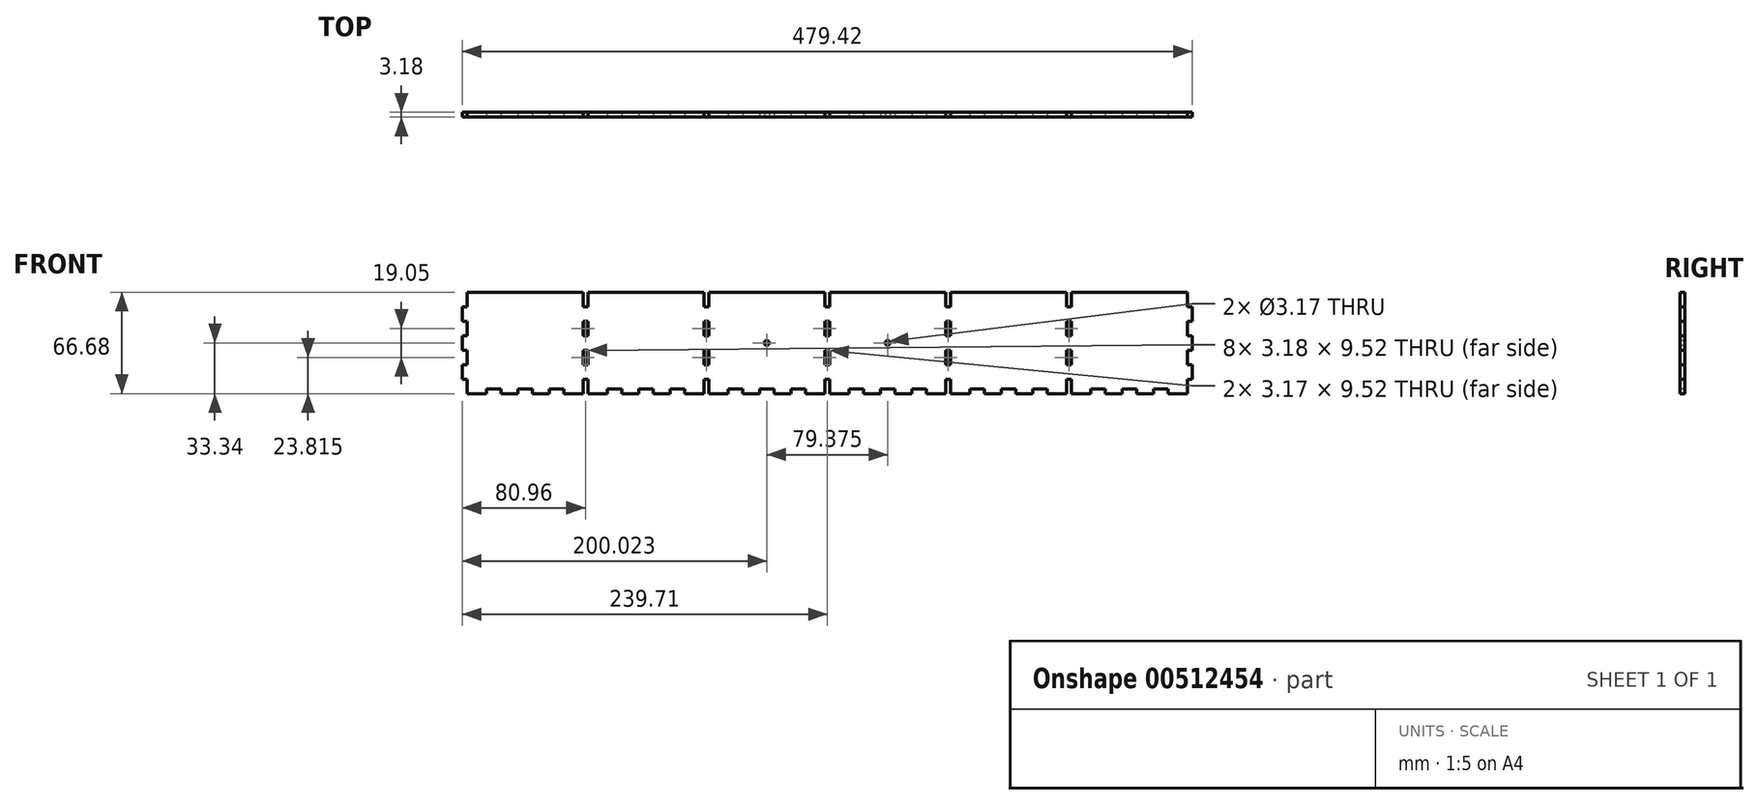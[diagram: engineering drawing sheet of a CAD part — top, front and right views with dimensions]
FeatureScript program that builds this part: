
annotation { "Feature Type Name" : "Feature", "Feature Type Description" : "" }
export const myFeature = defineFeature(function(context is Context, id is Id, definition is map)
    precondition{}
    {
        {
            var Q0;
            Q0=qCreatedBy(makeId("Front.planeOp"),FACE);
            var sketch = newSketch(context, id + "F0", { "sketchPlane" : qUnion([Q0])});
            skLineSegment(sketch, "E0.bottom", {"start": v(-239.71, 33.34) * mm, "end": v(239.71, 33.34) * mm});
            skLineSegment(sketch, "E0.top", {"start": v(-239.71, -33.34) * mm, "end": v(239.71, -33.34) * mm});
            skLineSegment(sketch, "E0.left", {"start": v(-239.71, 33.34) * mm, "end": v(-239.71, -33.34) * mm});
            skLineSegment(sketch, "E0.right", {"start": v(239.71, 33.34) * mm, "end": v(239.71, -33.34) * mm});
            skSolve(sketch);
        }
        {
            var Q0;
            Q0=makeQuery(id+"F0.imprint","IMPRINT",FACE,{"disambiguationData":[TD([[makeQuery(id+"F0.imprint","IMPRINT",EDGE,{"derivedFrom":sQuery(id+"F0.wireOp",EDGE,"E0.bottom")}),-1.0]])]});
            extrude(context, id + "F1", {"entities" : qUnion([Q0]), "depth" : 3.17 * mm});
        }
        {
            var Q0;
            Q0=makeQuery(id+"F1.opExtrude","CAP_FACE",FACE,{"disambiguationData":[OSD([sQuery(id+"F0.wireOp",EDGE,"E0.bottom"),sQuery(id+"F0.wireOp",EDGE,"E0.top"),sQuery(id+"F0.wireOp",EDGE,"E0.left"),sQuery(id+"F0.wireOp",EDGE,"E0.right")])],"isStart":false});
            var sketch = newSketch(context, id + "F2", { "sketchPlane" : qUnion([Q0])});
            skLineSegment(sketch, "E1.bottom", {"start": v(-239.71, -33.34) * mm, "end": v(-236.54, -33.34) * mm});
            skLineSegment(sketch, "E1.top", {"start": v(-239.71, -23.81) * mm, "end": v(-236.54, -23.81) * mm});
            skLineSegment(sketch, "E1.left", {"start": v(-239.71, -33.34) * mm, "end": v(-239.71, -23.81) * mm});
            skLineSegment(sketch, "E1.right", {"start": v(-236.54, -33.34) * mm, "end": v(-236.54, -23.81) * mm});
            skLineSegment(sketch, "E2.0.1.0", {"start": v(-236.54, -14.29) * mm, "end": v(-236.54, -4.76) * mm});
            skLineSegment(sketch, "E2.0.1.1", {"start": v(-239.71, -14.29) * mm, "end": v(-239.71, -4.76) * mm});
            skLineSegment(sketch, "E2.0.1.2", {"start": v(-239.71, -4.76) * mm, "end": v(-236.54, -4.76) * mm});
            skLineSegment(sketch, "E2.0.1.3", {"start": v(-239.71, -14.29) * mm, "end": v(-236.54, -14.29) * mm});
            skLineSegment(sketch, "E2.0.2.0", {"start": v(-236.54, 4.76) * mm, "end": v(-236.54, 14.29) * mm});
            skLineSegment(sketch, "E2.0.2.1", {"start": v(-239.71, 4.76) * mm, "end": v(-239.71, 14.29) * mm});
            skLineSegment(sketch, "E2.0.2.2", {"start": v(-239.71, 14.29) * mm, "end": v(-236.54, 14.29) * mm});
            skLineSegment(sketch, "E2.0.2.3", {"start": v(-239.71, 4.76) * mm, "end": v(-236.54, 4.76) * mm});
            skLineSegment(sketch, "E2.0.3.0", {"start": v(-236.54, 23.81) * mm, "end": v(-236.54, 33.34) * mm});
            skLineSegment(sketch, "E2.0.3.1", {"start": v(-239.71, 23.81) * mm, "end": v(-239.71, 33.34) * mm});
            skLineSegment(sketch, "E2.0.3.2", {"start": v(-239.71, 33.34) * mm, "end": v(-236.54, 33.34) * mm});
            skLineSegment(sketch, "E2.0.3.3", {"start": v(-239.71, 23.81) * mm, "end": v(-236.54, 23.81) * mm});
            skLineSegment(sketch, "E2.1.0.0", {"start": v(-157.16, -33.34) * mm, "end": v(-157.16, -23.81) * mm});
            skLineSegment(sketch, "E2.1.0.1", {"start": v(-160.34, -33.34) * mm, "end": v(-160.34, -23.81) * mm});
            skLineSegment(sketch, "E2.1.0.2", {"start": v(-160.34, -23.81) * mm, "end": v(-157.16, -23.81) * mm});
            skLineSegment(sketch, "E2.1.0.3", {"start": v(-160.34, -33.34) * mm, "end": v(-157.16, -33.34) * mm});
            skLineSegment(sketch, "E2.1.1.0", {"start": v(-157.16, -14.29) * mm, "end": v(-157.16, -4.76) * mm});
            skLineSegment(sketch, "E2.1.1.1", {"start": v(-160.34, -14.29) * mm, "end": v(-160.34, -4.76) * mm});
            skLineSegment(sketch, "E2.1.1.2", {"start": v(-160.34, -4.76) * mm, "end": v(-157.16, -4.76) * mm});
            skLineSegment(sketch, "E2.1.1.3", {"start": v(-160.34, -14.29) * mm, "end": v(-157.16, -14.29) * mm});
            skLineSegment(sketch, "E2.1.2.0", {"start": v(-157.16, 4.76) * mm, "end": v(-157.16, 14.29) * mm});
            skLineSegment(sketch, "E2.1.2.1", {"start": v(-160.34, 4.76) * mm, "end": v(-160.34, 14.29) * mm});
            skLineSegment(sketch, "E2.1.2.2", {"start": v(-160.34, 14.29) * mm, "end": v(-157.16, 14.29) * mm});
            skLineSegment(sketch, "E2.1.2.3", {"start": v(-160.34, 4.76) * mm, "end": v(-157.16, 4.76) * mm});
            skLineSegment(sketch, "E2.1.3.0", {"start": v(-157.16, 23.81) * mm, "end": v(-157.16, 33.34) * mm});
            skLineSegment(sketch, "E2.1.3.1", {"start": v(-160.34, 23.81) * mm, "end": v(-160.34, 33.34) * mm});
            skLineSegment(sketch, "E2.1.3.2", {"start": v(-160.34, 33.34) * mm, "end": v(-157.16, 33.34) * mm});
            skLineSegment(sketch, "E2.1.3.3", {"start": v(-160.34, 23.81) * mm, "end": v(-157.16, 23.81) * mm});
            skLineSegment(sketch, "E2.2.0.0", {"start": v(-77.79, -33.34) * mm, "end": v(-77.79, -23.81) * mm});
            skLineSegment(sketch, "E2.2.0.1", {"start": v(-80.96, -33.34) * mm, "end": v(-80.96, -23.81) * mm});
            skLineSegment(sketch, "E2.2.0.2", {"start": v(-80.96, -23.81) * mm, "end": v(-77.79, -23.81) * mm});
            skLineSegment(sketch, "E2.2.0.3", {"start": v(-80.96, -33.34) * mm, "end": v(-77.79, -33.34) * mm});
            skLineSegment(sketch, "E2.2.1.0", {"start": v(-77.79, -14.29) * mm, "end": v(-77.79, -4.76) * mm});
            skLineSegment(sketch, "E2.2.1.1", {"start": v(-80.96, -14.29) * mm, "end": v(-80.96, -4.76) * mm});
            skLineSegment(sketch, "E2.2.1.2", {"start": v(-80.96, -4.76) * mm, "end": v(-77.79, -4.76) * mm});
            skLineSegment(sketch, "E2.2.1.3", {"start": v(-80.96, -14.29) * mm, "end": v(-77.79, -14.29) * mm});
            skLineSegment(sketch, "E2.2.2.0", {"start": v(-77.79, 4.76) * mm, "end": v(-77.79, 14.29) * mm});
            skLineSegment(sketch, "E2.2.2.1", {"start": v(-80.96, 4.76) * mm, "end": v(-80.96, 14.29) * mm});
            skLineSegment(sketch, "E2.2.2.2", {"start": v(-80.96, 14.29) * mm, "end": v(-77.79, 14.29) * mm});
            skLineSegment(sketch, "E2.2.2.3", {"start": v(-80.96, 4.76) * mm, "end": v(-77.79, 4.76) * mm});
            skLineSegment(sketch, "E2.2.3.0", {"start": v(-77.79, 23.81) * mm, "end": v(-77.79, 33.34) * mm});
            skLineSegment(sketch, "E2.2.3.1", {"start": v(-80.96, 23.81) * mm, "end": v(-80.96, 33.34) * mm});
            skLineSegment(sketch, "E2.2.3.2", {"start": v(-80.96, 33.34) * mm, "end": v(-77.79, 33.34) * mm});
            skLineSegment(sketch, "E2.2.3.3", {"start": v(-80.96, 23.81) * mm, "end": v(-77.79, 23.81) * mm});
            skLineSegment(sketch, "E2.direction1", {"start": v(-239.71, -33.34) * mm, "end": v(-160.34, -33.34) * mm, "construction": true});
            skLineSegment(sketch, "E2.direction2", {"start": v(-239.71, -33.34) * mm, "end": v(-239.71, -14.29) * mm, "construction": true});
            skLineSegment(sketch, "E3.0.3.0", {"start": v(1.59, -33.34) * mm, "end": v(1.59, -23.81) * mm});
            skLineSegment(sketch, "E3.3.3.0", {"start": v(-1.59, -33.34) * mm, "end": v(-1.59, -23.81) * mm});
            skLineSegment(sketch, "E3.6.3.0", {"start": v(-1.59, -23.81) * mm, "end": v(1.59, -23.81) * mm});
            skLineSegment(sketch, "E3.9.3.0", {"start": v(-1.59, -33.34) * mm, "end": v(1.59, -33.34) * mm});
            skLineSegment(sketch, "E3.0.3.1", {"start": v(1.59, -14.29) * mm, "end": v(1.59, -4.76) * mm});
            skLineSegment(sketch, "E3.3.3.1", {"start": v(-1.59, -14.29) * mm, "end": v(-1.59, -4.76) * mm});
            skLineSegment(sketch, "E3.6.3.1", {"start": v(-1.59, -4.76) * mm, "end": v(1.59, -4.76) * mm});
            skLineSegment(sketch, "E3.9.3.1", {"start": v(-1.59, -14.29) * mm, "end": v(1.59, -14.29) * mm});
            skLineSegment(sketch, "E3.0.3.2", {"start": v(1.59, 4.76) * mm, "end": v(1.59, 14.29) * mm});
            skLineSegment(sketch, "E3.3.3.2", {"start": v(-1.59, 4.76) * mm, "end": v(-1.59, 14.29) * mm});
            skLineSegment(sketch, "E3.6.3.2", {"start": v(-1.59, 14.29) * mm, "end": v(1.59, 14.29) * mm});
            skLineSegment(sketch, "E3.9.3.2", {"start": v(-1.59, 4.76) * mm, "end": v(1.59, 4.76) * mm});
            skLineSegment(sketch, "E3.0.3.3", {"start": v(1.59, 23.81) * mm, "end": v(1.59, 33.34) * mm});
            skLineSegment(sketch, "E3.3.3.3", {"start": v(-1.59, 23.81) * mm, "end": v(-1.59, 33.34) * mm});
            skLineSegment(sketch, "E3.6.3.3", {"start": v(-1.59, 33.34) * mm, "end": v(1.59, 33.34) * mm});
            skLineSegment(sketch, "E3.9.3.3", {"start": v(-1.59, 23.81) * mm, "end": v(1.59, 23.81) * mm});
            skLineSegment(sketch, "E3.0.4.0", {"start": v(80.96, -33.34) * mm, "end": v(80.96, -23.81) * mm});
            skLineSegment(sketch, "E3.3.4.0", {"start": v(77.79, -33.34) * mm, "end": v(77.79, -23.81) * mm});
            skLineSegment(sketch, "E3.6.4.0", {"start": v(77.79, -23.81) * mm, "end": v(80.96, -23.81) * mm});
            skLineSegment(sketch, "E3.9.4.0", {"start": v(77.79, -33.34) * mm, "end": v(80.96, -33.34) * mm});
            skLineSegment(sketch, "E3.0.4.1", {"start": v(80.96, -14.29) * mm, "end": v(80.96, -4.76) * mm});
            skLineSegment(sketch, "E3.3.4.1", {"start": v(77.79, -14.29) * mm, "end": v(77.79, -4.76) * mm});
            skLineSegment(sketch, "E3.6.4.1", {"start": v(77.79, -4.76) * mm, "end": v(80.96, -4.76) * mm});
            skLineSegment(sketch, "E3.9.4.1", {"start": v(77.79, -14.29) * mm, "end": v(80.96, -14.29) * mm});
            skLineSegment(sketch, "E3.0.4.2", {"start": v(80.96, 4.76) * mm, "end": v(80.96, 14.29) * mm});
            skLineSegment(sketch, "E3.3.4.2", {"start": v(77.79, 4.76) * mm, "end": v(77.79, 14.29) * mm});
            skLineSegment(sketch, "E3.6.4.2", {"start": v(77.79, 14.29) * mm, "end": v(80.96, 14.29) * mm});
            skLineSegment(sketch, "E3.9.4.2", {"start": v(77.79, 4.76) * mm, "end": v(80.96, 4.76) * mm});
            skLineSegment(sketch, "E3.0.4.3", {"start": v(80.96, 23.81) * mm, "end": v(80.96, 33.34) * mm});
            skLineSegment(sketch, "E3.3.4.3", {"start": v(77.79, 23.81) * mm, "end": v(77.79, 33.34) * mm});
            skLineSegment(sketch, "E3.6.4.3", {"start": v(77.79, 33.34) * mm, "end": v(80.96, 33.34) * mm});
            skLineSegment(sketch, "E3.9.4.3", {"start": v(77.79, 23.81) * mm, "end": v(80.96, 23.81) * mm});
            skLineSegment(sketch, "E3.0.5.0", {"start": v(160.34, -33.34) * mm, "end": v(160.34, -23.81) * mm});
            skLineSegment(sketch, "E3.3.5.0", {"start": v(157.16, -33.34) * mm, "end": v(157.16, -23.81) * mm});
            skLineSegment(sketch, "E3.6.5.0", {"start": v(157.16, -23.81) * mm, "end": v(160.34, -23.81) * mm});
            skLineSegment(sketch, "E3.9.5.0", {"start": v(157.16, -33.34) * mm, "end": v(160.34, -33.34) * mm});
            skLineSegment(sketch, "E3.0.5.1", {"start": v(160.34, -14.29) * mm, "end": v(160.34, -4.76) * mm});
            skLineSegment(sketch, "E3.3.5.1", {"start": v(157.16, -14.29) * mm, "end": v(157.16, -4.76) * mm});
            skLineSegment(sketch, "E3.6.5.1", {"start": v(157.16, -4.76) * mm, "end": v(160.34, -4.76) * mm});
            skLineSegment(sketch, "E3.9.5.1", {"start": v(157.16, -14.29) * mm, "end": v(160.34, -14.29) * mm});
            skLineSegment(sketch, "E3.0.5.2", {"start": v(160.34, 4.76) * mm, "end": v(160.34, 14.29) * mm});
            skLineSegment(sketch, "E3.3.5.2", {"start": v(157.16, 4.76) * mm, "end": v(157.16, 14.29) * mm});
            skLineSegment(sketch, "E3.6.5.2", {"start": v(157.16, 14.29) * mm, "end": v(160.34, 14.29) * mm});
            skLineSegment(sketch, "E3.9.5.2", {"start": v(157.16, 4.76) * mm, "end": v(160.34, 4.76) * mm});
            skLineSegment(sketch, "E3.0.5.3", {"start": v(160.34, 23.81) * mm, "end": v(160.34, 33.34) * mm});
            skLineSegment(sketch, "E3.3.5.3", {"start": v(157.16, 23.81) * mm, "end": v(157.16, 33.34) * mm});
            skLineSegment(sketch, "E3.6.5.3", {"start": v(157.16, 33.34) * mm, "end": v(160.34, 33.34) * mm});
            skLineSegment(sketch, "E3.9.5.3", {"start": v(157.16, 23.81) * mm, "end": v(160.34, 23.81) * mm});
            skLineSegment(sketch, "E3.0.6.0", {"start": v(239.71, -33.34) * mm, "end": v(239.71, -23.81) * mm});
            skLineSegment(sketch, "E3.3.6.0", {"start": v(236.54, -33.34) * mm, "end": v(236.54, -23.81) * mm});
            skLineSegment(sketch, "E3.6.6.0", {"start": v(236.54, -23.81) * mm, "end": v(239.71, -23.81) * mm});
            skLineSegment(sketch, "E3.9.6.0", {"start": v(236.54, -33.34) * mm, "end": v(239.71, -33.34) * mm});
            skLineSegment(sketch, "E3.0.6.1", {"start": v(239.71, -14.29) * mm, "end": v(239.71, -4.76) * mm});
            skLineSegment(sketch, "E3.3.6.1", {"start": v(236.54, -14.29) * mm, "end": v(236.54, -4.76) * mm});
            skLineSegment(sketch, "E3.6.6.1", {"start": v(236.54, -4.76) * mm, "end": v(239.71, -4.76) * mm});
            skLineSegment(sketch, "E3.9.6.1", {"start": v(236.54, -14.29) * mm, "end": v(239.71, -14.29) * mm});
            skLineSegment(sketch, "E3.0.6.2", {"start": v(239.71, 4.76) * mm, "end": v(239.71, 14.29) * mm});
            skLineSegment(sketch, "E3.3.6.2", {"start": v(236.54, 4.76) * mm, "end": v(236.54, 14.29) * mm});
            skLineSegment(sketch, "E3.6.6.2", {"start": v(236.54, 14.29) * mm, "end": v(239.71, 14.29) * mm});
            skLineSegment(sketch, "E3.9.6.2", {"start": v(236.54, 4.76) * mm, "end": v(239.71, 4.76) * mm});
            skLineSegment(sketch, "E3.0.6.3", {"start": v(239.71, 23.81) * mm, "end": v(239.71, 33.34) * mm});
            skLineSegment(sketch, "E3.3.6.3", {"start": v(236.54, 23.81) * mm, "end": v(236.54, 33.34) * mm});
            skLineSegment(sketch, "E3.6.6.3", {"start": v(236.54, 33.34) * mm, "end": v(239.71, 33.34) * mm});
            skLineSegment(sketch, "E3.9.6.3", {"start": v(236.54, 23.81) * mm, "end": v(239.71, 23.81) * mm});
            skSolve(sketch);
        }
        {
            var Q0;
            Q0=qSketchRegion(id+"F2",true);
            extrude(context, id + "F3", {"entities" : qUnion([Q0]), "operationType" : NewBodyOperationType.REMOVE, "endBound" : BoundingType.THROUGH_ALL, "oppositeDirection" : true, "depth" : 25.4 * mm});
        }
        {
            var Q0;
            Q0=makeQuery(id+"F1.opExtrude","CAP_FACE",FACE,{"disambiguationData":[OSD([sQuery(id+"F0.wireOp",EDGE,"E0.bottom"),sQuery(id+"F0.wireOp",EDGE,"E0.top"),sQuery(id+"F0.wireOp",EDGE,"E0.left"),sQuery(id+"F0.wireOp",EDGE,"E0.right")])],"isStart":false});
            var sketch = newSketch(context, id + "F4", { "sketchPlane" : qUnion([Q0])});
            skLineSegment(sketch, "E4.bottom", {"start": v(-223.84, -33.34) * mm, "end": v(-214.31, -33.34) * mm});
            skLineSegment(sketch, "E4.top", {"start": v(-223.84, -30.16) * mm, "end": v(-214.31, -30.16) * mm});
            skLineSegment(sketch, "E4.left", {"start": v(-223.84, -33.34) * mm, "end": v(-223.84, -30.16) * mm});
            skLineSegment(sketch, "E4.right", {"start": v(-214.31, -33.34) * mm, "end": v(-214.31, -30.16) * mm});
            skLineSegment(sketch, "E5.1.0.0", {"start": v(-193.68, -33.34) * mm, "end": v(-193.68, -30.16) * mm});
            skLineSegment(sketch, "E5.1.0.1", {"start": v(-203.2, -33.34) * mm, "end": v(-203.2, -30.16) * mm});
            skLineSegment(sketch, "E5.1.0.2", {"start": v(-203.2, -30.16) * mm, "end": v(-193.68, -30.16) * mm});
            skLineSegment(sketch, "E5.1.0.3", {"start": v(-203.2, -33.34) * mm, "end": v(-193.68, -33.34) * mm});
            skLineSegment(sketch, "E5.2.0.0", {"start": v(-173.04, -33.34) * mm, "end": v(-173.04, -30.16) * mm});
            skLineSegment(sketch, "E5.2.0.1", {"start": v(-182.56, -33.34) * mm, "end": v(-182.56, -30.16) * mm});
            skLineSegment(sketch, "E5.2.0.2", {"start": v(-182.56, -30.16) * mm, "end": v(-173.04, -30.16) * mm});
            skLineSegment(sketch, "E5.2.0.3", {"start": v(-182.56, -33.34) * mm, "end": v(-173.04, -33.34) * mm});
            skLineSegment(sketch, "E5.direction1", {"start": v(-223.84, -33.34) * mm, "end": v(-203.2, -33.34) * mm, "construction": true});
            skLineSegment(sketch, "E6.1.0.0", {"start": v(-144.46, -30.16) * mm, "end": v(-134.94, -30.16) * mm});
            skLineSegment(sketch, "E6.1.0.1", {"start": v(-144.46, -33.34) * mm, "end": v(-123.83, -33.34) * mm, "construction": true});
            skLineSegment(sketch, "E6.1.0.2", {"start": v(-123.83, -33.34) * mm, "end": v(-114.3, -33.34) * mm});
            skLineSegment(sketch, "E6.1.0.3", {"start": v(-103.19, -33.34) * mm, "end": v(-93.66, -33.34) * mm});
            skLineSegment(sketch, "E6.1.0.4", {"start": v(-123.83, -30.16) * mm, "end": v(-114.3, -30.16) * mm});
            skLineSegment(sketch, "E6.1.0.5", {"start": v(-103.19, -30.16) * mm, "end": v(-93.66, -30.16) * mm});
            skLineSegment(sketch, "E6.1.0.6", {"start": v(-144.46, -33.34) * mm, "end": v(-134.94, -33.34) * mm});
            skLineSegment(sketch, "E6.1.0.7", {"start": v(-134.94, -33.34) * mm, "end": v(-134.94, -30.16) * mm});
            skLineSegment(sketch, "E6.1.0.8", {"start": v(-144.46, -33.34) * mm, "end": v(-144.46, -30.16) * mm});
            skLineSegment(sketch, "E6.1.0.9", {"start": v(-103.19, -33.34) * mm, "end": v(-103.19, -30.16) * mm});
            skLineSegment(sketch, "E6.1.0.10", {"start": v(-123.83, -33.34) * mm, "end": v(-123.83, -30.16) * mm});
            skLineSegment(sketch, "E6.1.0.11", {"start": v(-93.66, -33.34) * mm, "end": v(-93.66, -30.16) * mm});
            skLineSegment(sketch, "E6.1.0.12", {"start": v(-114.3, -33.34) * mm, "end": v(-114.3, -30.16) * mm});
            skLineSegment(sketch, "E6.2.0.0", {"start": v(-65.09, -30.16) * mm, "end": v(-55.56, -30.16) * mm});
            skLineSegment(sketch, "E6.2.0.1", {"start": v(-65.09, -33.34) * mm, "end": v(-44.45, -33.34) * mm, "construction": true});
            skLineSegment(sketch, "E6.2.0.2", {"start": v(-44.45, -33.34) * mm, "end": v(-34.93, -33.34) * mm});
            skLineSegment(sketch, "E6.2.0.3", {"start": v(-23.81, -33.34) * mm, "end": v(-14.29, -33.34) * mm});
            skLineSegment(sketch, "E6.2.0.4", {"start": v(-44.45, -30.16) * mm, "end": v(-34.93, -30.16) * mm});
            skLineSegment(sketch, "E6.2.0.5", {"start": v(-23.81, -30.16) * mm, "end": v(-14.29, -30.16) * mm});
            skLineSegment(sketch, "E6.2.0.6", {"start": v(-65.09, -33.34) * mm, "end": v(-55.56, -33.34) * mm});
            skLineSegment(sketch, "E6.2.0.7", {"start": v(-55.56, -33.34) * mm, "end": v(-55.56, -30.16) * mm});
            skLineSegment(sketch, "E6.2.0.8", {"start": v(-65.09, -33.34) * mm, "end": v(-65.09, -30.16) * mm});
            skLineSegment(sketch, "E6.2.0.9", {"start": v(-23.81, -33.34) * mm, "end": v(-23.81, -30.16) * mm});
            skLineSegment(sketch, "E6.2.0.10", {"start": v(-44.45, -33.34) * mm, "end": v(-44.45, -30.16) * mm});
            skLineSegment(sketch, "E6.2.0.11", {"start": v(-14.29, -33.34) * mm, "end": v(-14.29, -30.16) * mm});
            skLineSegment(sketch, "E6.2.0.12", {"start": v(-34.93, -33.34) * mm, "end": v(-34.93, -30.16) * mm});
            skLineSegment(sketch, "E6.3.0.0", {"start": v(14.29, -30.16) * mm, "end": v(23.81, -30.16) * mm});
            skLineSegment(sketch, "E6.3.0.1", {"start": v(14.29, -33.34) * mm, "end": v(34.92, -33.34) * mm, "construction": true});
            skLineSegment(sketch, "E6.3.0.2", {"start": v(34.92, -33.34) * mm, "end": v(44.45, -33.34) * mm});
            skLineSegment(sketch, "E6.3.0.3", {"start": v(55.56, -33.34) * mm, "end": v(65.09, -33.34) * mm});
            skLineSegment(sketch, "E6.3.0.4", {"start": v(34.92, -30.16) * mm, "end": v(44.45, -30.16) * mm});
            skLineSegment(sketch, "E6.3.0.5", {"start": v(55.56, -30.16) * mm, "end": v(65.09, -30.16) * mm});
            skLineSegment(sketch, "E6.3.0.6", {"start": v(14.29, -33.34) * mm, "end": v(23.81, -33.34) * mm});
            skLineSegment(sketch, "E6.3.0.7", {"start": v(23.81, -33.34) * mm, "end": v(23.81, -30.16) * mm});
            skLineSegment(sketch, "E6.3.0.8", {"start": v(14.29, -33.34) * mm, "end": v(14.29, -30.16) * mm});
            skLineSegment(sketch, "E6.3.0.9", {"start": v(55.56, -33.34) * mm, "end": v(55.56, -30.16) * mm});
            skLineSegment(sketch, "E6.3.0.10", {"start": v(34.92, -33.34) * mm, "end": v(34.92, -30.16) * mm});
            skLineSegment(sketch, "E6.3.0.11", {"start": v(65.09, -33.34) * mm, "end": v(65.09, -30.16) * mm});
            skLineSegment(sketch, "E6.3.0.12", {"start": v(44.45, -33.34) * mm, "end": v(44.45, -30.16) * mm});
            skLineSegment(sketch, "E6.4.0.0", {"start": v(93.66, -30.16) * mm, "end": v(103.19, -30.16) * mm});
            skLineSegment(sketch, "E6.4.0.1", {"start": v(93.66, -33.34) * mm, "end": v(114.3, -33.34) * mm, "construction": true});
            skLineSegment(sketch, "E6.4.0.2", {"start": v(114.3, -33.34) * mm, "end": v(123.82, -33.34) * mm});
            skLineSegment(sketch, "E6.4.0.3", {"start": v(134.94, -33.34) * mm, "end": v(144.46, -33.34) * mm});
            skLineSegment(sketch, "E6.4.0.4", {"start": v(114.3, -30.16) * mm, "end": v(123.82, -30.16) * mm});
            skLineSegment(sketch, "E6.4.0.5", {"start": v(134.94, -30.16) * mm, "end": v(144.46, -30.16) * mm});
            skLineSegment(sketch, "E6.4.0.6", {"start": v(93.66, -33.34) * mm, "end": v(103.19, -33.34) * mm});
            skLineSegment(sketch, "E6.4.0.7", {"start": v(103.19, -33.34) * mm, "end": v(103.19, -30.16) * mm});
            skLineSegment(sketch, "E6.4.0.8", {"start": v(93.66, -33.34) * mm, "end": v(93.66, -30.16) * mm});
            skLineSegment(sketch, "E6.4.0.9", {"start": v(134.94, -33.34) * mm, "end": v(134.94, -30.16) * mm});
            skLineSegment(sketch, "E6.4.0.10", {"start": v(114.3, -33.34) * mm, "end": v(114.3, -30.16) * mm});
            skLineSegment(sketch, "E6.4.0.11", {"start": v(144.46, -33.34) * mm, "end": v(144.46, -30.16) * mm});
            skLineSegment(sketch, "E6.4.0.12", {"start": v(123.82, -33.34) * mm, "end": v(123.82, -30.16) * mm});
            skLineSegment(sketch, "E6.5.0.0", {"start": v(173.04, -30.16) * mm, "end": v(182.56, -30.16) * mm});
            skLineSegment(sketch, "E6.5.0.1", {"start": v(173.04, -33.34) * mm, "end": v(193.67, -33.34) * mm, "construction": true});
            skLineSegment(sketch, "E6.5.0.2", {"start": v(193.67, -33.34) * mm, "end": v(203.2, -33.34) * mm});
            skLineSegment(sketch, "E6.5.0.3", {"start": v(214.31, -33.34) * mm, "end": v(223.84, -33.34) * mm});
            skLineSegment(sketch, "E6.5.0.4", {"start": v(193.67, -30.16) * mm, "end": v(203.2, -30.16) * mm});
            skLineSegment(sketch, "E6.5.0.5", {"start": v(214.31, -30.16) * mm, "end": v(223.84, -30.16) * mm});
            skLineSegment(sketch, "E6.5.0.6", {"start": v(173.04, -33.34) * mm, "end": v(182.56, -33.34) * mm});
            skLineSegment(sketch, "E6.5.0.7", {"start": v(182.56, -33.34) * mm, "end": v(182.56, -30.16) * mm});
            skLineSegment(sketch, "E6.5.0.8", {"start": v(173.04, -33.34) * mm, "end": v(173.04, -30.16) * mm});
            skLineSegment(sketch, "E6.5.0.9", {"start": v(214.31, -33.34) * mm, "end": v(214.31, -30.16) * mm});
            skLineSegment(sketch, "E6.5.0.10", {"start": v(193.67, -33.34) * mm, "end": v(193.67, -30.16) * mm});
            skLineSegment(sketch, "E6.5.0.11", {"start": v(223.84, -33.34) * mm, "end": v(223.84, -30.16) * mm});
            skLineSegment(sketch, "E6.5.0.12", {"start": v(203.2, -33.34) * mm, "end": v(203.2, -30.16) * mm});
            skLineSegment(sketch, "E6.direction1", {"start": v(-223.84, -33.34) * mm, "end": v(-144.46, -33.34) * mm, "construction": true});
            skSolve(sketch);
        }
        {
            var Q0;
            Q0=qSketchRegion(id+"F4",true);
            extrude(context, id + "F5", {"entities" : qUnion([Q0]), "operationType" : NewBodyOperationType.REMOVE, "endBound" : BoundingType.THROUGH_ALL, "oppositeDirection" : true, "depth" : 25.4 * mm});
        }
        {
            var Q0;
            Q0=makeQuery(id+"F1.opExtrude","CAP_FACE",FACE,{"disambiguationData":[OSD([sQuery(id+"F0.wireOp",EDGE,"E0.bottom"),sQuery(id+"F0.wireOp",EDGE,"E0.top"),sQuery(id+"F0.wireOp",EDGE,"E0.left"),sQuery(id+"F0.wireOp",EDGE,"E0.right")])],"isStart":false});
            var sketch = newSketch(context, id + "F6", { "sketchPlane" : qUnion([Q0])});
            skCircle(sketch, "E7", {"center": v(-39.69, 0) * mm, "radius": 1.59 * mm});
            skCircle(sketch, "E8.1.0.0", {"center": v(39.69, 0) * mm, "radius": 1.59 * mm});
            skLineSegment(sketch, "E8.direction1", {"start": v(-39.69, 0) * mm, "end": v(39.69, 0) * mm, "construction": true});
            skSolve(sketch);
        }
        {
            var Q0;
            Q0 = qSketchRegion(id + "F6", true);
            extrude(context, id + "F7", {"entities" : qUnion([Q0]), "operationType" : NewBodyOperationType.REMOVE, "endBound" : BoundingType.THROUGH_ALL, "oppositeDirection" : true, "depth" : 25.4 * mm});
        }
    });
